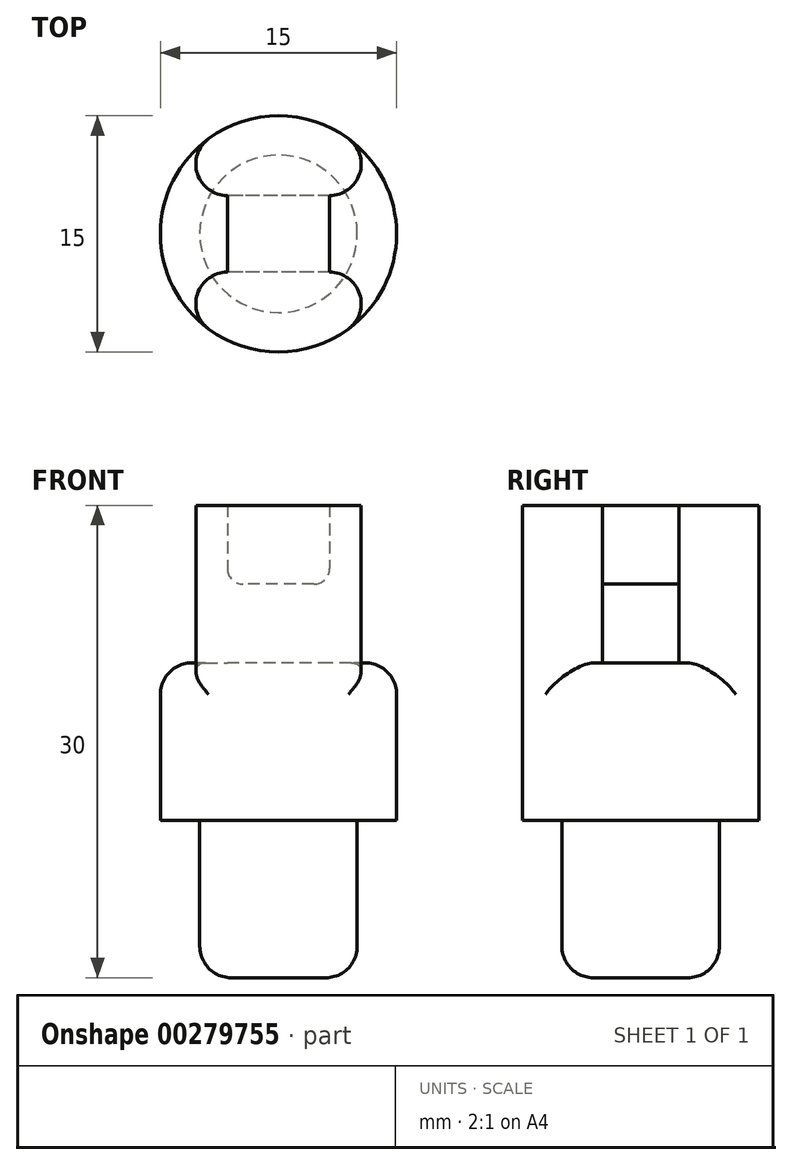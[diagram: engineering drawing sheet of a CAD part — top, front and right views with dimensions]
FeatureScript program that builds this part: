
annotation { "Feature Type Name" : "Feature", "Feature Type Description" : "" }
export const myFeature = defineFeature(function(context is Context, id is Id, definition is map)
    precondition{}
    {
        {
            var Q0;
            Q0=qCreatedBy(makeId("Top.planeOp"),FACE);
            var sketch = newSketch(context, id + "F0", { "sketchPlane" : qUnion([Q0])});
            skCircle(sketch, "E0", {"center": v(0, 0) * mm, "radius": 5 * mm});
            skSolve(sketch);
        }
        {
            var Q0;
            Q0 = qSketchRegion(id + "F0", true);
            extrude(context, id + "F1", {"entities" : qUnion([Q0]), "depth" : 10 * mm});
        }
        {
            var Q0;
            Q0=makeQuery(id+"F1.opExtrude","CAP_FACE",FACE,{"disambiguationData":[OSD([sQuery(id+"F0.wireOp",EDGE,"E0")])],"isStart":false});
            var sketch = newSketch(context, id + "F2", { "sketchPlane" : qUnion([Q0])});
            skCircle(sketch, "E1", {"center": v(0, 0) * mm, "radius": 7.5 * mm});
            skSolve(sketch);
        }
        {
            var Q0;
            Q0=makeQuery(id+"F2.imprint","IMPRINT",FACE,{"disambiguationData":[TD([[makeQuery(id+"F2.imprint","IMPRINT",EDGE,{"derivedFrom":makeQuery(id+"F1.opExtrude","CAP_EDGE",EDGE,{"disambiguationData":[OSD([sQuery(id+"F0.wireOp",EDGE,"E0")])],"isStart":false})}),1.0]])]});
            var Q1;
            Q1=makeQuery(id+"F2.imprint","IMPRINT",FACE,{"disambiguationData":[TD([[makeQuery(id+"F2.imprint","IMPRINT",EDGE,{"derivedFrom":sQuery(id+"F2.wireOp",EDGE,"E1")}),1.0]])]});
            extrude(context, id + "F3", {"entities" : qUnion([Q0, Q1]), "operationType" : NewBodyOperationType.ADD, "depth" : 15 * mm});
        }
        {
            var Q0;
            Q0=makeQuery(id+"F3.opExtrude","CAP_FACE",FACE,{"disambiguationData":[OSD([sQuery(id+"F2.wireOp",EDGE,"E1")])],"isStart":false});
            var sketch = newSketch(context, id + "F4", { "sketchPlane" : qUnion([Q0])});
            skLineSegment(sketch, "E2.bottom", {"start": v(10.12, -2.44) * mm, "end": v(-10.12, -2.44) * mm});
            skLineSegment(sketch, "E2.top", {"start": v(10.12, 2.44) * mm, "end": v(-10.12, 2.44) * mm});
            skLineSegment(sketch, "E2.left", {"start": v(10.12, -2.44) * mm, "end": v(10.12, 2.44) * mm});
            skLineSegment(sketch, "E2.right", {"start": v(-10.12, -2.44) * mm, "end": v(-10.12, 2.44) * mm});
            skPoint(sketch, "E2.middle", {"position": v(0, 0) * mm});
            skSolve(sketch);
        }
        {
            var Q0;
            {var subQ0=sQuery(id+"F4.wireOp",EDGE,"E2.right");Q0=makeQuery(id+"F4.imprint","IMPRINT",FACE,{"disambiguationData":[TD([[makeQuery(id+"F4.imprint","IMPRINT",EDGE,{"derivedFrom":subQ0}),-1.0]])]});}
            var Q1;
            {var subQ0=sQuery(id+"F4.wireOp",EDGE,"E2.bottom");var subQ1=makeQuery(id+"F3.opExtrude","CAP_EDGE",EDGE,{"disambiguationData":[OSD([sQuery(id+"F2.wireOp",EDGE,"E1")])],"isStart":false});var subQ2=makeQuery(id+"F4.imprint","INTERSECT",VERTEX,{"disambiguationData":[OD(0.0)],"derivedFrom":[subQ1,subQ0]});Q1=makeQuery(id+"F4.imprint","IMPRINT",FACE,{"disambiguationData":[TD([[makeQuery(id+"F4.imprint","IMPRINT",EDGE,{"disambiguationData":[TD([[subQ2,-1.0]])],"derivedFrom":subQ0}),-1.0]])]});}
            var Q2;
            {var subQ0=sQuery(id+"F4.wireOp",EDGE,"E2.left");Q2=makeQuery(id+"F4.imprint","IMPRINT",FACE,{"disambiguationData":[TD([[makeQuery(id+"F4.imprint","IMPRINT",EDGE,{"derivedFrom":subQ0}),1.0]])]});}
            extrude(context, id + "F5", {"entities" : qUnion([Q0, Q1, Q2]), "operationType" : NewBodyOperationType.REMOVE, "oppositeDirection" : true, "depth" : 5 * mm});
        }
        {
            var Q0;
            Q0=makeQuery(id+"F5.boolean.opBoolean","INTERSECT",EDGE,{"disambiguationData":[OD(1.0)],"derivedFrom":[makeQuery(id+"F3.opExtrude","SWEPT_FACE",FACE,{"disambiguationData":[OSD([sQuery(id+"F2.wireOp",EDGE,"E1")])]}),makeQuery(id+"F5.opExtrude","CAP_FACE",FACE,{"disambiguationData":[OSD([sQuery(id+"F4.wireOp",EDGE,"E2.bottom"),sQuery(id+"F4.wireOp",EDGE,"E2.top"),sQuery(id+"F4.wireOp",EDGE,"E2.left"),sQuery(id+"F4.wireOp",EDGE,"E2.right")])],"isStart":false})]});
            var Q1;
            Q1=makeQuery(id+"F5.boolean.opBoolean","INTERSECT",EDGE,{"disambiguationData":[OD(0.0)],"derivedFrom":[makeQuery(id+"F3.opExtrude","SWEPT_FACE",FACE,{"disambiguationData":[OSD([sQuery(id+"F2.wireOp",EDGE,"E1")])]}),makeQuery(id+"F5.opExtrude","CAP_FACE",FACE,{"disambiguationData":[OSD([sQuery(id+"F4.wireOp",EDGE,"E2.bottom"),sQuery(id+"F4.wireOp",EDGE,"E2.top"),sQuery(id+"F4.wireOp",EDGE,"E2.left"),sQuery(id+"F4.wireOp",EDGE,"E2.right")])],"isStart":false})]});
            var Q2;
            Q2=makeQuery(id+"F5.boolean.opBoolean","INTERSECT",EDGE,{"disambiguationData":[OD(0.0)],"derivedFrom":[makeQuery(id+"F3.opExtrude","SWEPT_FACE",FACE,{"disambiguationData":[OSD([sQuery(id+"F2.wireOp",EDGE,"E1")])]}),makeQuery(id+"F5.opExtrude","SWEPT_FACE",FACE,{"disambiguationData":[OSD([sQuery(id+"F4.wireOp",EDGE,"E2.top")])]})]});
            var Q3;
            Q3=makeQuery(id+"F5.boolean.opBoolean","INTERSECT",EDGE,{"disambiguationData":[OD(0.0)],"derivedFrom":[makeQuery(id+"F3.opExtrude","SWEPT_FACE",FACE,{"disambiguationData":[OSD([sQuery(id+"F2.wireOp",EDGE,"E1")])]}),makeQuery(id+"F5.opExtrude","SWEPT_FACE",FACE,{"disambiguationData":[OSD([sQuery(id+"F4.wireOp",EDGE,"E2.bottom")])]})]});
            var Q4;
            Q4=makeQuery(id+"F5.boolean.opBoolean","INTERSECT",EDGE,{"disambiguationData":[OD(1.0)],"derivedFrom":[makeQuery(id+"F3.opExtrude","SWEPT_FACE",FACE,{"disambiguationData":[OSD([sQuery(id+"F2.wireOp",EDGE,"E1")])]}),makeQuery(id+"F5.opExtrude","SWEPT_FACE",FACE,{"disambiguationData":[OSD([sQuery(id+"F4.wireOp",EDGE,"E2.top")])]})]});
            var Q5;
            Q5=makeQuery(id+"F5.boolean.opBoolean","INTERSECT",EDGE,{"disambiguationData":[OD(1.0)],"derivedFrom":[makeQuery(id+"F3.opExtrude","SWEPT_FACE",FACE,{"disambiguationData":[OSD([sQuery(id+"F2.wireOp",EDGE,"E1")])]}),makeQuery(id+"F5.opExtrude","SWEPT_FACE",FACE,{"disambiguationData":[OSD([sQuery(id+"F4.wireOp",EDGE,"E2.bottom")])]})]});
            fillet(context, id + "F6", {"entities" : qUnion([Q0, Q1, Q2, Q3, Q4, Q5]), "radius" : 2 * mm, "tangentPropagation" : true, "allowEdgeOverflow" : false});
        }
        {
            var Q0;
            Q0=makeQuery(id+"F1.opExtrude","CAP_EDGE",EDGE,{"disambiguationData":[OSD([sQuery(id+"F0.wireOp",EDGE,"E0")])],"isStart":true});
            fillet(context, id + "F7", {"entities" : qUnion([Q0]), "radius" : 2 * mm, "tangentPropagation" : true, "allowEdgeOverflow" : false});
        }
        {
            var Q0;
            {var subQ0=sQuery(id+"F2.wireOp",EDGE,"E1");Q0=makeQuery(id+"F5.boolean.opBoolean","SPLIT",FACE,{"disambiguationData":[TD([makeQuery(id+"F5.opExtrude","SWEPT_FACE",FACE,{"disambiguationData":[OSD([sQuery(id+"F4.wireOp",EDGE,"E2.top")])]})])],"derivedFrom":makeQuery(id+"F3.opExtrude","CAP_FACE",FACE,{"disambiguationData":[OSD([subQ0])],"isStart":false})});}
            var Q1;
            {var subQ0=sQuery(id+"F2.wireOp",EDGE,"E1");Q1=makeQuery(id+"F5.boolean.opBoolean","SPLIT",FACE,{"disambiguationData":[TD([makeQuery(id+"F5.opExtrude","SWEPT_FACE",FACE,{"disambiguationData":[OSD([sQuery(id+"F4.wireOp",EDGE,"E2.bottom")])]})])],"derivedFrom":makeQuery(id+"F3.opExtrude","CAP_FACE",FACE,{"disambiguationData":[OSD([subQ0])],"isStart":false})});}
            extrude(context, id + "F8", {"entities" : qUnion([Q0, Q1]), "operationType" : NewBodyOperationType.ADD, "depth" : 5 * mm});
        }
        {
            var Q0;
            {var subQ0=sQuery(id+"F4.wireOp",EDGE,"E2.top");Q0=makeQuery(id+"F8.boolean.opBoolean","MERGE",FACE,{"derivedFrom":[makeQuery(id+"F5.boolean.opBoolean","COPY",FACE,{"derivedFrom":makeQuery(id+"F5.opExtrude","SWEPT_FACE",FACE,{"disambiguationData":[OSD([subQ0])]})}),makeQuery(id+"F8.opExtrude","SWEPT_FACE",FACE,{"disambiguationData":[OSD([subQ0])]})]});}
            var sketch = newSketch(context, id + "F9", { "sketchPlane" : qUnion([Q0])});
            skLineSegment(sketch, "E3", {"start": v(3.25, 25) * mm, "end": v(-3.25, 25) * mm});
            skSolve(sketch);
        }
        {
            var Q0;
            {var subQ0=sQuery(id+"F9.wireOp",EDGE,"E3");Q0=makeQuery(id+"F9.imprint","IMPRINT",FACE,{"disambiguationData":[TD([[makeQuery(id+"F9.imprint","IMPRINT",EDGE,{"derivedFrom":subQ0}),-1.0]])]});}
            extrude(context, id + "F10", {"entities" : qUnion([Q0]), "operationType" : NewBodyOperationType.ADD, "depth" : 6 * mm});
        }
        {
            var Q0;
            {var subQ0=sQuery(id+"F9.wireOp",EDGE,"E3");var subQ1=sQuery(id+"F2.wireOp",EDGE,"E1");var subQ2=makeQuery(id+"F3.opExtrude","SWEPT_FACE",FACE,{"disambiguationData":[OSD([subQ1])]});var subQ3=sQuery(id+"F4.wireOp",EDGE,"E2.top");var subQ4=makeQuery(id+"F5.opExtrude","SWEPT_FACE",FACE,{"disambiguationData":[OSD([subQ3])]});var subQ5=makeQuery(id+"F5.boolean.opBoolean","COPY",FACE,{"derivedFrom":subQ4});var subQ6=makeQuery(id+"F5.boolean.opBoolean","INTERSECT",EDGE,{"disambiguationData":[OD(1.0)],"derivedFrom":[subQ2,subQ4]});Q0=makeQuery(id+"F10.opExtrude","SWEPT_EDGE",EDGE,{"disambiguationData":[OSD([subQ1,subQ3,subQ0]),TDD([makeQuery(id+"F9.imprint","INTERSECT",VERTEX,{"derivedFrom":[makeQuery(id+"F8.boolean.opBoolean","MERGE",EDGE,{"derivedFrom":[makeQuery(id+"F6.opFillet","BLEND_EDGE",EDGE,{"blendedFrom":[subQ6,subQ5],"blendedInto":[subQ5]}),makeQuery(id+"F8.opExtrude","SWEPT_EDGE",EDGE,{"disambiguationData":[OSD([subQ1,subQ3]),TDD([makeQuery(id+"F6.opFillet","BLEND_VERTEX",VERTEX,{"blendedFrom":[subQ6,subQ5,makeQuery(id+"F5.boolean.opBoolean","SPLIT",FACE,{"disambiguationData":[TD([subQ4])],"derivedFrom":makeQuery(id+"F3.opExtrude","CAP_FACE",FACE,{"disambiguationData":[OSD([subQ1])],"isStart":false})})],"blendedInto":[subQ5,makeQuery(id+"F5.boolean.opBoolean","SPLIT",FACE,{"disambiguationData":[TD([subQ4])],"derivedFrom":makeQuery(id+"F3.opExtrude","CAP_FACE",FACE,{"disambiguationData":[OSD([subQ1])],"isStart":false})})]})])]})]}),subQ0]})])]});}
            var Q1;
            {var subQ0=sQuery(id+"F9.wireOp",EDGE,"E3");var subQ1=sQuery(id+"F2.wireOp",EDGE,"E1");var subQ2=makeQuery(id+"F3.opExtrude","SWEPT_FACE",FACE,{"disambiguationData":[OSD([subQ1])]});var subQ3=sQuery(id+"F4.wireOp",EDGE,"E2.top");var subQ4=makeQuery(id+"F5.opExtrude","SWEPT_FACE",FACE,{"disambiguationData":[OSD([subQ3])]});var subQ5=makeQuery(id+"F5.boolean.opBoolean","COPY",FACE,{"derivedFrom":subQ4});var subQ6=makeQuery(id+"F5.boolean.opBoolean","INTERSECT",EDGE,{"disambiguationData":[OD(0.0)],"derivedFrom":[subQ2,subQ4]});Q1=makeQuery(id+"F10.opExtrude","SWEPT_EDGE",EDGE,{"disambiguationData":[OSD([subQ1,subQ3,subQ0]),TDD([makeQuery(id+"F9.imprint","INTERSECT",VERTEX,{"derivedFrom":[makeQuery(id+"F8.boolean.opBoolean","MERGE",EDGE,{"derivedFrom":[makeQuery(id+"F6.opFillet","BLEND_EDGE",EDGE,{"blendedFrom":[subQ6,subQ5],"blendedInto":[subQ5]}),makeQuery(id+"F8.opExtrude","SWEPT_EDGE",EDGE,{"disambiguationData":[OSD([subQ1,subQ3]),TDD([makeQuery(id+"F6.opFillet","BLEND_VERTEX",VERTEX,{"blendedFrom":[subQ6,subQ5,makeQuery(id+"F5.boolean.opBoolean","SPLIT",FACE,{"disambiguationData":[TD([subQ4])],"derivedFrom":makeQuery(id+"F3.opExtrude","CAP_FACE",FACE,{"disambiguationData":[OSD([subQ1])],"isStart":false})})],"blendedInto":[subQ5,makeQuery(id+"F5.boolean.opBoolean","SPLIT",FACE,{"disambiguationData":[TD([subQ4])],"derivedFrom":makeQuery(id+"F3.opExtrude","CAP_FACE",FACE,{"disambiguationData":[OSD([subQ1])],"isStart":false})})]})])]})]}),subQ0]})])]});}
            fillet(context, id + "F11", {"entities" : qUnion([Q0, Q1]), "radius" : 1 * mm, "tangentPropagation" : true, "allowEdgeOverflow" : false});
        }
    });
